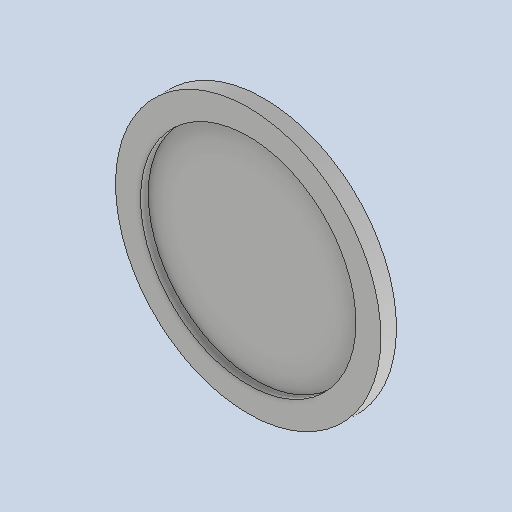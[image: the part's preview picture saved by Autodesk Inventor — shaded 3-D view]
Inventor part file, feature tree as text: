
AUTODESK INVENTOR PART (.ipt)
format: ipt  version: 2025 (Build 290162010, 162A)  size: 243,200 bytes
history: native  units: mm
features: extrude x2, sketch x2
ambient origin geometry x8: Origin, YZ Plane, XZ Plane, XY Plane, X Axis, Y Axis, Z Axis, Center Point
bodies: Solid1 (feature_tree)
feature tree (4):
  extrude  "Extrusion1"  Depth=10.0mm TaperAngle=0.0deg
  extrude  "Extrusion2"  Depth=5.0mm TaperAngle=0.0deg
  sketch  "Sketch1"  dims[d0=170.0mm d1=10.0mm d2=0.0mm]
  sketch  "Sketch2"  dims[d3=138.0mm d4=5.0mm d5=0.0mm]
